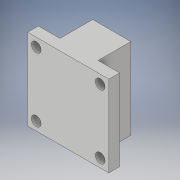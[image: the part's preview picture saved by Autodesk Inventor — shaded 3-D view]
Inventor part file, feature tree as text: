
AUTODESK INVENTOR PART (.ipt)
format: ipt  version: 2019.3 (Build 233278000, 278)  size: 144,896 bytes
history: native  units: mm
features: extrude x3, sketch x3, other x3, reference x2
ambient origin geometry x8: Origin, YZ Plane, XZ Plane, XY Plane, X Axis, Y Axis, Z Axis, Center Point
bodies: Solid1 (feature_tree)
feature tree (11):
  extrude  "Extrusion1"  Depth=10.0mm TaperAngle=0.0deg
  extrude  "Extrusion2"  Depth=25.0mm
  extrude  "Extrusion4"  Depth=35.4mm
  sketch  "Sketch1"  dims[d0=25.0mm d4=10.0mm d5=0.0mm]
  reference  "Reference1"
  reference  "Reference2"
  sketch  "Sketch3"  dims[d19=30.4mm d20=0.0mm d31=25.0mm]
  sketch  "Sketch5"  dims[d32=5.0mm d33=9.0mm d34=9.0mm d35=9.0mm d36=9.0mm d37=8.0mm d38=8.0mm d39=8.0mm d40=8.0mm d41=8.0mm d42=8.0mm d43=8.0mm d44=8.0mm d45=35.4mm d46=20.0mm d47=5.0mm d48=5.0mm d49=25.4mm d50=25.4mm d51=35.4mm d52=0.0mm]
  parser-record x1  (decoder bookkeeping rows leaked as tree rows — omitted from the tree; the rows remain in map.json)
  other  "Assembly.iam"
  other  "LateralBars:1"
note: 1 file-system path scrubbed to <path> (originals preserved in map.json)
